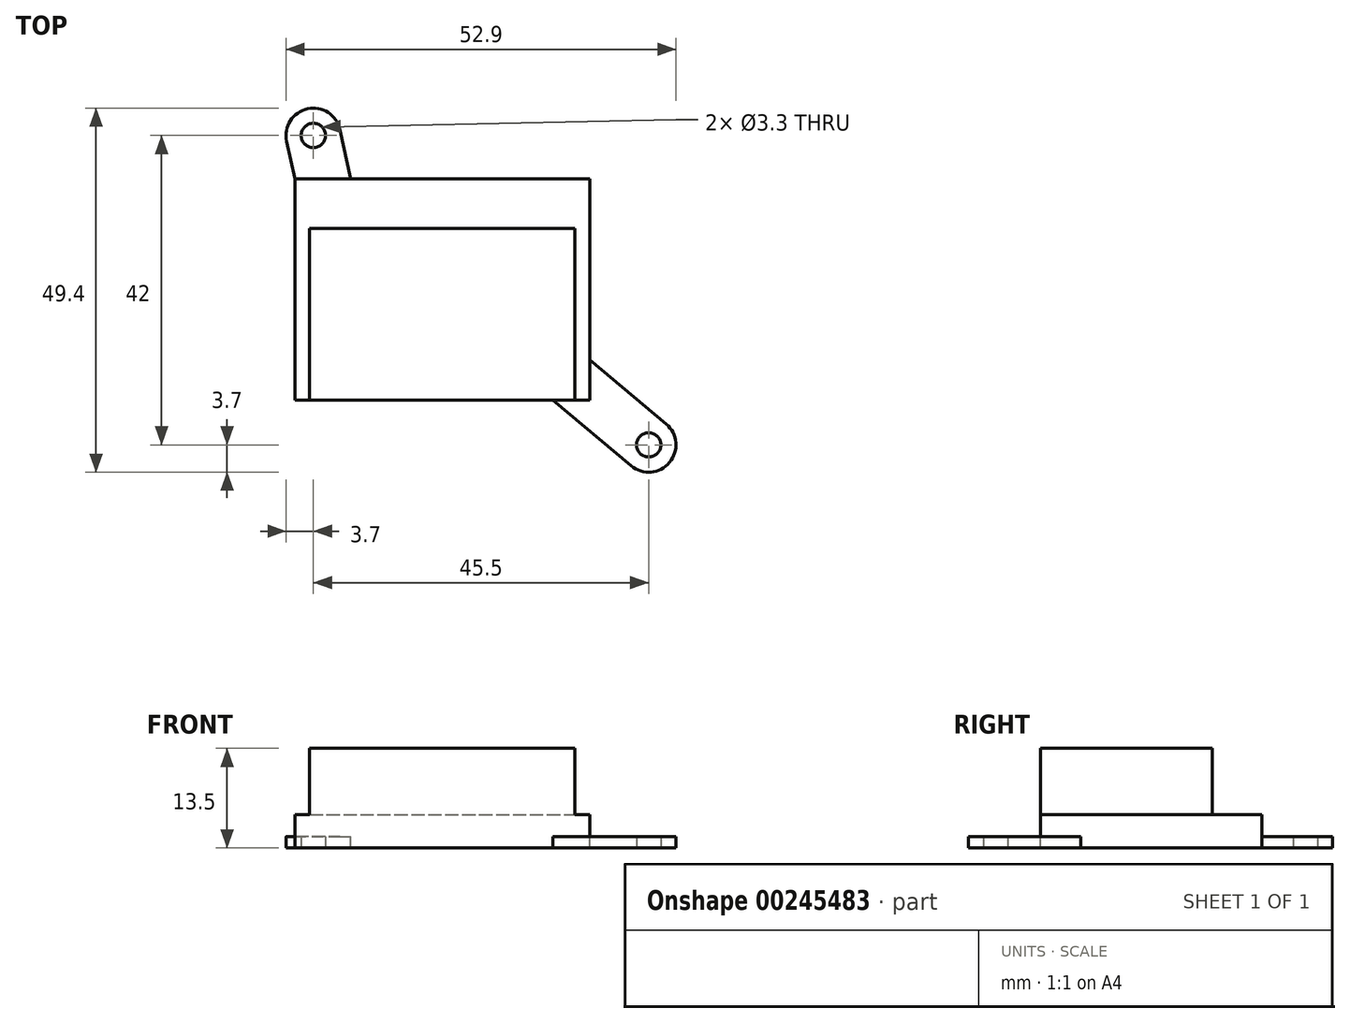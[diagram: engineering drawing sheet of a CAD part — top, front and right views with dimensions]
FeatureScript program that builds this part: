
annotation { "Feature Type Name" : "Feature", "Feature Type Description" : "" }
export const myFeature = defineFeature(function(context is Context, id is Id, definition is map)
    precondition{}
    {
        {
            var Q0;
            Q0=qCreatedBy(makeId("Top.planeOp"),FACE);
            var sketch = newSketch(context, id + "F0", { "sketchPlane" : qUnion([Q0])});
            skLineSegment(sketch, "E0", {"start": v(0, 0) * mm, "end": v(65, 0) * mm});
            skLineSegment(sketch, "E1", {"start": v(32.5, 0) * mm, "end": v(32.5, 107.14) * mm, "construction": true});
            skPoint(sketch, "E2", {"position": v(65.73, 14) * mm});
            skLineSegment(sketch, "E3", {"start": v(65, 0) * mm, "end": v(65.49, 28) * mm, "construction": true});
            skPoint(sketch, "E4.orphan", {"position": v(66.47, 28) * mm});
            skArc(sketch, "E5", {"start": v(65, 0) * mm, "mid": v(65.73, 14) * mm, "end": v(65.49, 28) * mm});
            skLineSegment(sketch, "E6", {"start": v(65.49, 28) * mm, "end": v(57.3, 50.5) * mm});
            skPoint(sketch, "E7", {"position": v(32.5, 63.5) * mm});
            skArc(sketch, "E8.MirrorCS", {"start": v(0, 0) * mm, "mid": v(-0.73, 14) * mm, "end": v(-0.49, 28) * mm});
            skLineSegment(sketch, "E9.MirrorCS", {"start": v(-0.49, 28) * mm, "end": v(7.7, 50.5) * mm});
            skLineSegment(sketch, "E10.MirrorCS", {"start": v(0, 0) * mm, "end": v(-0.49, 28) * mm, "construction": true});
            skPoint(sketch, "E11.MirrorP", {"position": v(-1.47, 28) * mm});
            skPoint(sketch, "E12.MirrorP", {"position": v(-0.73, 14) * mm});
            skArc(sketch, "E13", {"start": v(57.3, 50.5) * mm, "mid": v(32.5, 63.5) * mm, "end": v(7.7, 50.5) * mm});
            skCircle(sketch, "E14", {"center": v(4.5, 12.5) * mm, "radius": 1.65 * mm});
            skCircle(sketch, "E15.MirrorC", {"center": v(60.5, 12.5) * mm, "radius": 1.65 * mm});
            skCircle(sketch, "E16", {"center": v(15, 54.5) * mm, "radius": 1.65 * mm});
            skLineSegment(sketch, "E17", {"start": v(65.73, 14) * mm, "end": v(65.24, 14) * mm});
            skLineSegment(sketch, "E18", {"start": v(-0.73, 14) * mm, "end": v(-0.24, 14) * mm});
            skSolve(sketch);
        }
        {
            var Q0;
            Q0=qSketchRegion(id+"F0",true);
            extrude(context, id + "F1", {"entities" : qUnion([Q0]), "depth" : 1.5 * mm});
        }
        {
            var Q0;
            Q0=makeQuery(id+"F1.opExtrude","CAP_FACE",FACE,{"disambiguationData":[OSD([sQuery(id+"F0.wireOp",EDGE,"E0"),sQuery(id+"F0.wireOp",EDGE,"E5"),sQuery(id+"F0.wireOp",EDGE,"E6"),sQuery(id+"F0.wireOp",EDGE,"E8.MirrorCS"),sQuery(id+"F0.wireOp",EDGE,"E9.MirrorCS"),sQuery(id+"F0.wireOp",EDGE,"E13"),sQuery(id+"F0.wireOp",EDGE,"E14"),sQuery(id+"F0.wireOp",EDGE,"E15.MirrorC"),sQuery(id+"F0.wireOp",EDGE,"E16")])],"isStart":false});
            var sketch = newSketch(context, id + "F2", { "sketchPlane" : qUnion([Q0])});
            skCircle(sketch, "E19", {"center": v(15, 54.5) * mm, "radius": 3.7 * mm});
            skCircle(sketch, "E20", {"center": v(4.5, 12.5) * mm, "radius": 3.7 * mm});
            skCircle(sketch, "E21", {"center": v(60.5, 12.5) * mm, "radius": 3.7 * mm});
            skLineSegment(sketch, "E22.bottom", {"start": v(12.5, 18.6) * mm, "end": v(52.5, 18.6) * mm});
            skLineSegment(sketch, "E22.top", {"start": v(12.5, 48.6) * mm, "end": v(52.5, 48.6) * mm});
            skLineSegment(sketch, "E22.left", {"start": v(12.5, 18.6) * mm, "end": v(12.5, 48.6) * mm});
            skLineSegment(sketch, "E22.right", {"start": v(52.5, 18.6) * mm, "end": v(52.5, 48.6) * mm});
            skPoint(sketch, "E22.middle", {"position": v(32.5, 33.6) * mm});
            skPoint(sketch, "E22.middle.positionSnap0", {"position": v(32.5, 0) * mm});
            skPoint(sketch, "E22.centerSnap0", {"position": v(32.5, 0) * mm});
            skLineSegment(sketch, "E23", {"start": v(12.5, 48.6) * mm, "end": v(11.39, 53.71) * mm});
            skLineSegment(sketch, "E24", {"start": v(18.61, 55.29) * mm, "end": v(20.07, 48.6) * mm});
            skLineSegment(sketch, "E25", {"start": v(62.88, 15.33) * mm, "end": v(52.5, 24.06) * mm});
            skLineSegment(sketch, "E26", {"start": v(58.12, 9.67) * mm, "end": v(47.5, 18.6) * mm});
            skLineSegment(sketch, "E27", {"start": v(2.12, 15.33) * mm, "end": v(12.5, 24.06) * mm});
            skLineSegment(sketch, "E28", {"start": v(6.88, 9.67) * mm, "end": v(17.5, 18.6) * mm});
            skSolve(sketch);
        }
        {
            var Q0;
            {var subQ1=sQuery(id+"F2.wireOp",EDGE,"E23");Q0=makeQuery(id+"F2.imprint","IMPRINT",FACE,{"disambiguationData":[TD([[makeQuery(id+"F2.imprint","IMPRINT",EDGE,{"derivedFrom":subQ1}),1.0]])]});}
            extrude(context, id + "F3", {"entities" : qUnion([Q0]), "operationType" : NewBodyOperationType.REMOVE, "endBound" : BoundingType.THROUGH_ALL, "oppositeDirection" : true, "depth" : 25 * mm});
        }
        {
            var Q0;
            {var subQ0=sQuery(id+"F2.wireOp",EDGE,"E19");var subQ1=makeQuery(id+"F1.opExtrude","CAP_EDGE",EDGE,{"disambiguationData":[OSD([sQuery(id+"F0.wireOp",EDGE,"E13")])],"isStart":false});var subQ2=makeQuery(id+"F2.imprint","INTERSECT",VERTEX,{"disambiguationData":[OD(0.0)],"derivedFrom":[subQ1,subQ0]});Q0=makeQuery(id+"F2.imprint","IMPRINT",FACE,{"disambiguationData":[TD([[makeQuery(id+"F2.imprint","IMPRINT",EDGE,{"disambiguationData":[TD([[subQ2,-1.0]])],"derivedFrom":subQ0}),1.0]])]});}
            extrude(context, id + "F4", {"entities" : qUnion([Q0]), "operationType" : NewBodyOperationType.ADD, "oppositeDirection" : true, "depth" : 1.5 * mm});
        }
        {
            var Q0;
            {var subQ0=sQuery(id+"F0.wireOp",EDGE,"E13");Q0=makeQuery(id+"F4.boolean.opBoolean","MERGE",FACE,{"derivedFrom":[makeQuery(id+"F1.opExtrude","CAP_FACE",FACE,{"disambiguationData":[OSD([sQuery(id+"F0.wireOp",EDGE,"E0"),sQuery(id+"F0.wireOp",EDGE,"E5"),sQuery(id+"F0.wireOp",EDGE,"E6"),sQuery(id+"F0.wireOp",EDGE,"E8.MirrorCS"),sQuery(id+"F0.wireOp",EDGE,"E9.MirrorCS"),subQ0,sQuery(id+"F0.wireOp",EDGE,"E14"),sQuery(id+"F0.wireOp",EDGE,"E15.MirrorC"),sQuery(id+"F0.wireOp",EDGE,"E16")])],"isStart":false}),makeQuery(id+"F4.opExtrude","CAP_FACE",FACE,{"disambiguationData":[OSD([subQ0,sQuery(id+"F2.wireOp",EDGE,"E19")])],"isStart":true})]});}
            var sketch = newSketch(context, id + "F5", { "sketchPlane" : qUnion([Q0])});
            skLineSegment(sketch, "E29.bottom", {"start": v(12.5, 18.6) * mm, "end": v(52.5, 18.6) * mm});
            skLineSegment(sketch, "E29.top", {"start": v(12.5, 48.6) * mm, "end": v(52.5, 48.6) * mm});
            skLineSegment(sketch, "E29.left", {"start": v(12.5, 18.6) * mm, "end": v(12.5, 48.6) * mm});
            skLineSegment(sketch, "E29.right", {"start": v(52.5, 18.6) * mm, "end": v(52.5, 48.6) * mm});
            skSolve(sketch);
        }
        {
            var Q0;
            Q0=qSketchRegion(id+"F5",true);
            extrude(context, id + "F6", {"entities" : qUnion([Q0]), "operationType" : NewBodyOperationType.ADD, "depth" : 3 * mm});
        }
        {
            var Q0;
            Q0=makeQuery(id+"F6.opExtrude","CAP_FACE",FACE,{"disambiguationData":[OSD([sQuery(id+"F5.wireOp",EDGE,"E29.bottom"),sQuery(id+"F5.wireOp",EDGE,"E29.top"),sQuery(id+"F5.wireOp",EDGE,"E29.left"),sQuery(id+"F5.wireOp",EDGE,"E29.right")])],"isStart":false});
            var sketch = newSketch(context, id + "F7", { "sketchPlane" : qUnion([Q0])});
            skLineSegment(sketch, "E30.bottom", {"start": v(14.5, 18.6) * mm, "end": v(50.5, 18.6) * mm});
            skLineSegment(sketch, "E30.top", {"start": v(14.5, 41.9) * mm, "end": v(50.5, 41.9) * mm});
            skLineSegment(sketch, "E30.left", {"start": v(14.5, 18.6) * mm, "end": v(14.5, 41.9) * mm});
            skLineSegment(sketch, "E30.right", {"start": v(50.5, 18.6) * mm, "end": v(50.5, 41.9) * mm});
            skSolve(sketch);
        }
        {
            var Q0;
            Q0=qSketchRegion(id+"F7",true);
            extrude(context, id + "F8", {"entities" : qUnion([Q0]), "operationType" : NewBodyOperationType.ADD, "depth" : 9 * mm});
        }
        {
            var Q0;
            {var subQ0=sQuery(id+"F0.wireOp",EDGE,"E14");var subQ1=sQuery(id+"F0.wireOp",EDGE,"E13");Q0=makeQuery(id+"F6.boolean.opBoolean","SPLIT",FACE,{"disambiguationData":[TD([makeQuery(id+"F1.opExtrude","SWEPT_FACE",FACE,{"disambiguationData":[OSD([subQ0])]})])],"derivedFrom":makeQuery(id+"F4.boolean.opBoolean","MERGE",FACE,{"derivedFrom":[makeQuery(id+"F1.opExtrude","CAP_FACE",FACE,{"disambiguationData":[OSD([sQuery(id+"F0.wireOp",EDGE,"E0"),sQuery(id+"F0.wireOp",EDGE,"E5"),sQuery(id+"F0.wireOp",EDGE,"E6"),sQuery(id+"F0.wireOp",EDGE,"E8.MirrorCS"),sQuery(id+"F0.wireOp",EDGE,"E9.MirrorCS"),subQ1,subQ0,sQuery(id+"F0.wireOp",EDGE,"E15.MirrorC"),sQuery(id+"F0.wireOp",EDGE,"E16")])],"isStart":false}),makeQuery(id+"F4.opExtrude","CAP_FACE",FACE,{"disambiguationData":[OSD([subQ1,sQuery(id+"F2.wireOp",EDGE,"E19")])],"isStart":true})]})});}
            var sketch = newSketch(context, id + "F9", { "sketchPlane" : qUnion([Q0])});
            skCircle(sketch, "E31", {"center": v(4.5, 12.5) * mm, "radius": 3.75 * mm});
            skLineSegment(sketch, "E32", {"start": v(17.5, 18.6) * mm, "end": v(6.88, 9.67) * mm});
            skLineSegment(sketch, "E33", {"start": v(2.12, 15.33) * mm, "end": v(12.5, 24.06) * mm});
            skLineSegment(sketch, "E34", {"start": v(12.5, 24.06) * mm, "end": v(12.5, 18.6) * mm});
            skLineSegment(sketch, "E35", {"start": v(12.5, 18.6) * mm, "end": v(17.5, 18.6) * mm});
            skSolve(sketch);
        }
        {
            var Q0;
            Q0 = qSketchRegion(id + "F9", true);
            extrude(context, id + "F10", {"entities" : qUnion([Q0]), "operationType" : NewBodyOperationType.REMOVE, "endBound" : BoundingType.THROUGH_ALL, "oppositeDirection" : true, "depth" : 25 * mm});
        }
    });
